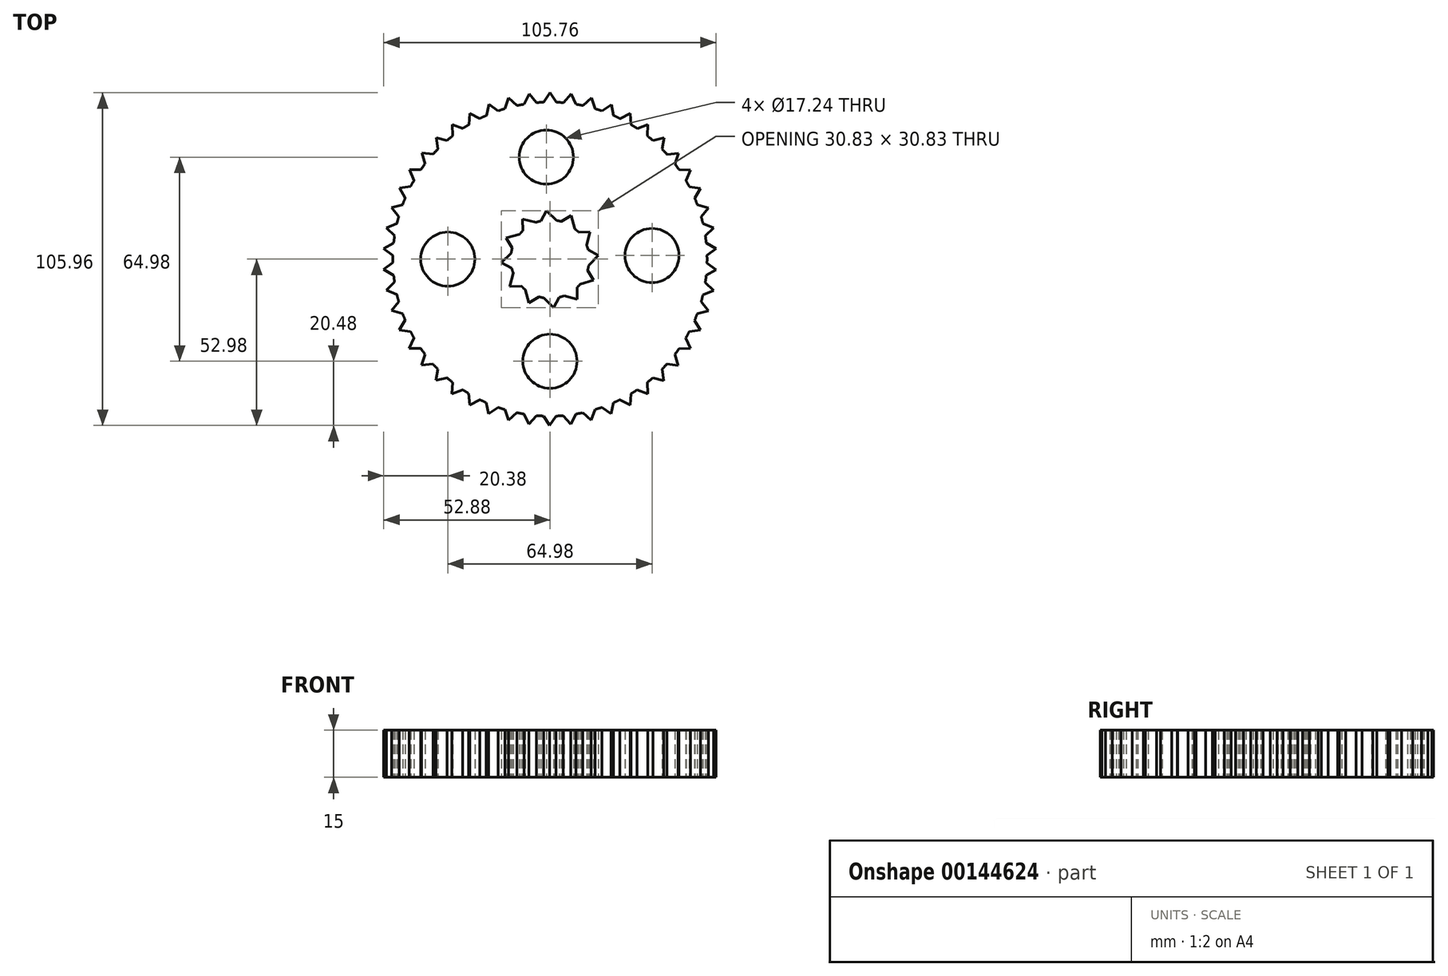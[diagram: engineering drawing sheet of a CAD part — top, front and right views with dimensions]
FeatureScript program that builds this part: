
annotation { "Feature Type Name" : "Feature", "Feature Type Description" : "" }
export const myFeature = defineFeature(function(context is Context, id is Id, definition is map)
    precondition{}
    {
        {
            var Q0;
            Q0=qCreatedBy(makeId("Top.planeOp"),FACE);
            var sketch = newSketch(context, id + "F0", { "sketchPlane" : qUnion([Q0])});
            skArc(sketch, "E0", {"start": v(-1.97, 49.96) * mm, "mid": v(-3.12, 49.9) * mm, "end": v(-4.26, 49.82) * mm});
            skLineSegment(sketch, "E1", {"start": v(-1.97, 49.96) * mm, "end": v(0.05, 52.98) * mm});
            skLineSegment(sketch, "E2", {"start": v(0.05, 52.98) * mm, "end": v(2.02, 49.96) * mm});
            skLineSegment(sketch, "E3.1.0", {"start": v(-8.22, 49.32) * mm, "end": v(-6.6, 52.57) * mm});
            skLineSegment(sketch, "E3.1.1", {"start": v(-6.6, 52.57) * mm, "end": v(-4.26, 49.82) * mm});
            skLineSegment(sketch, "E3.2.0", {"start": v(-14.34, 47.9) * mm, "end": v(-13.13, 51.33) * mm});
            skLineSegment(sketch, "E3.2.1", {"start": v(-13.13, 51.33) * mm, "end": v(-10.47, 48.9) * mm});
            skLineSegment(sketch, "E3.3.0", {"start": v(-20.23, 45.73) * mm, "end": v(-19.46, 49.28) * mm});
            skLineSegment(sketch, "E3.3.1", {"start": v(-19.46, 49.28) * mm, "end": v(-16.51, 47.2) * mm});
            skLineSegment(sketch, "E3.4.0", {"start": v(-25.8, 42.83) * mm, "end": v(-25.48, 46.45) * mm});
            skLineSegment(sketch, "E3.4.1", {"start": v(-25.48, 46.45) * mm, "end": v(-22.3, 44.75) * mm});
            skLineSegment(sketch, "E3.5.0", {"start": v(-30.96, 39.26) * mm, "end": v(-31.1, 42.89) * mm});
            skLineSegment(sketch, "E3.5.1", {"start": v(-31.1, 42.89) * mm, "end": v(-27.73, 41.6) * mm});
            skLineSegment(sketch, "E3.6.0", {"start": v(-35.64, 35.07) * mm, "end": v(-36.23, 38.65) * mm});
            skLineSegment(sketch, "E3.6.1", {"start": v(-36.23, 38.65) * mm, "end": v(-32.73, 37.8) * mm});
            skLineSegment(sketch, "E3.7.0", {"start": v(-39.75, 30.33) * mm, "end": v(-40.8, 33.8) * mm});
            skLineSegment(sketch, "E3.7.1", {"start": v(-40.8, 33.8) * mm, "end": v(-37.2, 33.4) * mm});
            skLineSegment(sketch, "E3.8.0", {"start": v(-43.24, 25.1) * mm, "end": v(-44.7, 28.43) * mm});
            skLineSegment(sketch, "E3.8.1", {"start": v(-44.7, 28.43) * mm, "end": v(-41.1, 28.47) * mm});
            skLineSegment(sketch, "E3.9.0", {"start": v(-46.05, 19.49) * mm, "end": v(-47.92, 22.6) * mm});
            skLineSegment(sketch, "E3.9.1", {"start": v(-47.92, 22.6) * mm, "end": v(-44.34, 23.1) * mm});
            skLineSegment(sketch, "E3.10.0", {"start": v(-48.13, 13.56) * mm, "end": v(-50.37, 16.42) * mm});
            skLineSegment(sketch, "E3.10.1", {"start": v(-50.37, 16.42) * mm, "end": v(-46.9, 17.36) * mm});
            skLineSegment(sketch, "E3.11.0", {"start": v(-49.45, 7.42) * mm, "end": v(-52.03, 9.97) * mm});
            skLineSegment(sketch, "E3.11.1", {"start": v(-52.03, 9.97) * mm, "end": v(-48.7, 11.34) * mm});
            skLineSegment(sketch, "E3.12.0", {"start": v(-49.99, 1.17) * mm, "end": v(-52.87, 3.37) * mm});
            skLineSegment(sketch, "E3.12.1", {"start": v(-52.87, 3.37) * mm, "end": v(-49.73, 5.15) * mm});
            skLineSegment(sketch, "E3.13.0", {"start": v(-49.74, -5.1) * mm, "end": v(-52.88, -3.28) * mm});
            skLineSegment(sketch, "E3.13.1", {"start": v(-52.88, -3.28) * mm, "end": v(-49.99, -1.12) * mm});
            skLineSegment(sketch, "E3.14.0", {"start": v(-48.7, -11.3) * mm, "end": v(-52.05, -9.88) * mm});
            skLineSegment(sketch, "E3.14.1", {"start": v(-52.05, -9.88) * mm, "end": v(-49.45, -7.38) * mm});
            skLineSegment(sketch, "E3.15.0", {"start": v(-46.9, -17.32) * mm, "end": v(-50.4, -16.33) * mm});
            skLineSegment(sketch, "E3.15.1", {"start": v(-50.4, -16.33) * mm, "end": v(-48.14, -13.52) * mm});
            skLineSegment(sketch, "E3.16.0", {"start": v(-44.37, -23.06) * mm, "end": v(-47.96, -22.52) * mm});
            skLineSegment(sketch, "E3.16.1", {"start": v(-47.96, -22.52) * mm, "end": v(-46.06, -19.44) * mm});
            skLineSegment(sketch, "E3.17.0", {"start": v(-41.13, -28.44) * mm, "end": v(-44.76, -28.35) * mm});
            skLineSegment(sketch, "E3.17.1", {"start": v(-44.76, -28.35) * mm, "end": v(-43.26, -25.06) * mm});
            skLineSegment(sketch, "E3.18.0", {"start": v(-37.24, -33.37) * mm, "end": v(-40.85, -33.74) * mm});
            skLineSegment(sketch, "E3.18.1", {"start": v(-40.85, -33.74) * mm, "end": v(-39.78, -30.29) * mm});
            skLineSegment(sketch, "E3.19.0", {"start": v(-32.76, -37.77) * mm, "end": v(-36.3, -38.6) * mm});
            skLineSegment(sketch, "E3.19.1", {"start": v(-36.3, -38.6) * mm, "end": v(-35.67, -35.04) * mm});
            skLineSegment(sketch, "E3.20.0", {"start": v(-27.77, -41.58) * mm, "end": v(-31.18, -42.84) * mm});
            skLineSegment(sketch, "E3.20.1", {"start": v(-31.18, -42.84) * mm, "end": v(-31, -39.23) * mm});
            skLineSegment(sketch, "E3.21.0", {"start": v(-22.34, -44.73) * mm, "end": v(-25.56, -46.4) * mm});
            skLineSegment(sketch, "E3.21.1", {"start": v(-25.56, -46.4) * mm, "end": v(-25.84, -42.8) * mm});
            skLineSegment(sketch, "E3.22.0", {"start": v(-16.56, -47.18) * mm, "end": v(-19.55, -49.24) * mm});
            skLineSegment(sketch, "E3.22.1", {"start": v(-19.55, -49.24) * mm, "end": v(-20.27, -45.7) * mm});
            skLineSegment(sketch, "E3.23.0", {"start": v(-10.51, -48.88) * mm, "end": v(-13.22, -51.3) * mm});
            skLineSegment(sketch, "E3.23.1", {"start": v(-13.22, -51.3) * mm, "end": v(-14.38, -47.89) * mm});
            skLineSegment(sketch, "E3.24.0", {"start": v(-4.3, -49.81) * mm, "end": v(-6.69, -52.56) * mm});
            skLineSegment(sketch, "E3.24.1", {"start": v(-6.69, -52.56) * mm, "end": v(-8.26, -49.31) * mm});
            skLineSegment(sketch, "E3.25.0", {"start": v(1.97, -49.96) * mm, "end": v(-0.05, -52.98) * mm});
            skLineSegment(sketch, "E3.25.1", {"start": v(-0.05, -52.98) * mm, "end": v(-2.02, -49.96) * mm});
            skLineSegment(sketch, "E3.26.0", {"start": v(8.22, -49.32) * mm, "end": v(6.6, -52.57) * mm});
            skLineSegment(sketch, "E3.26.1", {"start": v(6.6, -52.57) * mm, "end": v(4.26, -49.82) * mm});
            skLineSegment(sketch, "E3.27.0", {"start": v(14.34, -47.9) * mm, "end": v(13.13, -51.33) * mm});
            skLineSegment(sketch, "E3.27.1", {"start": v(13.13, -51.33) * mm, "end": v(10.47, -48.9) * mm});
            skLineSegment(sketch, "E3.28.0", {"start": v(20.23, -45.73) * mm, "end": v(19.46, -49.28) * mm});
            skLineSegment(sketch, "E3.28.1", {"start": v(19.46, -49.28) * mm, "end": v(16.51, -47.2) * mm});
            skLineSegment(sketch, "E3.29.0", {"start": v(25.8, -42.83) * mm, "end": v(25.48, -46.45) * mm});
            skLineSegment(sketch, "E3.29.1", {"start": v(25.48, -46.45) * mm, "end": v(22.3, -44.75) * mm});
            skLineSegment(sketch, "E3.30.0", {"start": v(30.96, -39.26) * mm, "end": v(31.1, -42.89) * mm});
            skLineSegment(sketch, "E3.30.1", {"start": v(31.1, -42.89) * mm, "end": v(27.73, -41.6) * mm});
            skLineSegment(sketch, "E3.31.0", {"start": v(35.64, -35.07) * mm, "end": v(36.23, -38.65) * mm});
            skLineSegment(sketch, "E3.31.1", {"start": v(36.23, -38.65) * mm, "end": v(32.73, -37.8) * mm});
            skLineSegment(sketch, "E3.32.0", {"start": v(39.75, -30.33) * mm, "end": v(40.8, -33.8) * mm});
            skLineSegment(sketch, "E3.32.1", {"start": v(40.8, -33.8) * mm, "end": v(37.2, -33.4) * mm});
            skLineSegment(sketch, "E3.33.0", {"start": v(43.24, -25.1) * mm, "end": v(44.7, -28.43) * mm});
            skLineSegment(sketch, "E3.33.1", {"start": v(44.7, -28.43) * mm, "end": v(41.1, -28.47) * mm});
            skLineSegment(sketch, "E3.34.0", {"start": v(46.05, -19.49) * mm, "end": v(47.92, -22.6) * mm});
            skLineSegment(sketch, "E3.34.1", {"start": v(47.92, -22.6) * mm, "end": v(44.34, -23.1) * mm});
            skLineSegment(sketch, "E3.35.0", {"start": v(48.13, -13.56) * mm, "end": v(50.37, -16.42) * mm});
            skLineSegment(sketch, "E3.35.1", {"start": v(50.37, -16.42) * mm, "end": v(46.9, -17.36) * mm});
            skLineSegment(sketch, "E3.36.0", {"start": v(49.45, -7.42) * mm, "end": v(52.03, -9.97) * mm});
            skLineSegment(sketch, "E3.36.1", {"start": v(52.03, -9.97) * mm, "end": v(48.7, -11.34) * mm});
            skLineSegment(sketch, "E3.37.0", {"start": v(49.99, -1.17) * mm, "end": v(52.87, -3.37) * mm});
            skLineSegment(sketch, "E3.37.1", {"start": v(52.87, -3.37) * mm, "end": v(49.73, -5.15) * mm});
            skLineSegment(sketch, "E3.38.0", {"start": v(49.74, 5.1) * mm, "end": v(52.88, 3.28) * mm});
            skLineSegment(sketch, "E3.38.1", {"start": v(52.88, 3.28) * mm, "end": v(49.99, 1.12) * mm});
            skLineSegment(sketch, "E3.39.0", {"start": v(48.7, 11.3) * mm, "end": v(52.05, 9.88) * mm});
            skLineSegment(sketch, "E3.39.1", {"start": v(52.05, 9.88) * mm, "end": v(49.45, 7.38) * mm});
            skLineSegment(sketch, "E3.40.0", {"start": v(46.9, 17.32) * mm, "end": v(50.4, 16.33) * mm});
            skLineSegment(sketch, "E3.40.1", {"start": v(50.4, 16.33) * mm, "end": v(48.14, 13.52) * mm});
            skLineSegment(sketch, "E3.41.0", {"start": v(44.37, 23.06) * mm, "end": v(47.96, 22.52) * mm});
            skLineSegment(sketch, "E3.41.1", {"start": v(47.96, 22.52) * mm, "end": v(46.06, 19.44) * mm});
            skLineSegment(sketch, "E3.42.0", {"start": v(41.13, 28.44) * mm, "end": v(44.76, 28.35) * mm});
            skLineSegment(sketch, "E3.42.1", {"start": v(44.76, 28.35) * mm, "end": v(43.26, 25.06) * mm});
            skLineSegment(sketch, "E3.43.0", {"start": v(37.24, 33.37) * mm, "end": v(40.85, 33.74) * mm});
            skLineSegment(sketch, "E3.43.1", {"start": v(40.85, 33.74) * mm, "end": v(39.78, 30.29) * mm});
            skLineSegment(sketch, "E3.44.0", {"start": v(32.76, 37.77) * mm, "end": v(36.3, 38.6) * mm});
            skLineSegment(sketch, "E3.44.1", {"start": v(36.3, 38.6) * mm, "end": v(35.67, 35.04) * mm});
            skLineSegment(sketch, "E3.45.0", {"start": v(27.77, 41.58) * mm, "end": v(31.18, 42.84) * mm});
            skLineSegment(sketch, "E3.45.1", {"start": v(31.18, 42.84) * mm, "end": v(31, 39.23) * mm});
            skLineSegment(sketch, "E3.46.0", {"start": v(22.34, 44.73) * mm, "end": v(25.56, 46.4) * mm});
            skLineSegment(sketch, "E3.46.1", {"start": v(25.56, 46.4) * mm, "end": v(25.84, 42.8) * mm});
            skLineSegment(sketch, "E3.47.0", {"start": v(16.56, 47.18) * mm, "end": v(19.55, 49.24) * mm});
            skLineSegment(sketch, "E3.47.1", {"start": v(19.55, 49.24) * mm, "end": v(20.27, 45.7) * mm});
            skLineSegment(sketch, "E3.48.0", {"start": v(10.51, 48.88) * mm, "end": v(13.22, 51.3) * mm});
            skLineSegment(sketch, "E3.48.1", {"start": v(13.22, 51.3) * mm, "end": v(14.38, 47.89) * mm});
            skLineSegment(sketch, "E3.49.0", {"start": v(4.3, 49.81) * mm, "end": v(6.69, 52.56) * mm});
            skLineSegment(sketch, "E3.49.1", {"start": v(6.69, 52.56) * mm, "end": v(8.26, 49.31) * mm});
            skArc(sketch, "E4.trimOffspring", {"start": v(4.3, 49.81) * mm, "mid": v(3.16, 49.9) * mm, "end": v(2.02, 49.96) * mm});
            skArc(sketch, "E5.trimOffspring", {"start": v(10.51, 48.88) * mm, "mid": v(9.4, 49.11) * mm, "end": v(8.26, 49.31) * mm});
            skArc(sketch, "E6.trimOffspring", {"start": v(16.56, 47.18) * mm, "mid": v(15.47, 47.55) * mm, "end": v(14.38, 47.89) * mm});
            skArc(sketch, "E7.trimOffspring", {"start": v(-8.22, 49.32) * mm, "mid": v(-9.35, 49.12) * mm, "end": v(-10.47, 48.9) * mm});
            skArc(sketch, "E8.trimOffspring", {"start": v(-14.34, 47.9) * mm, "mid": v(-15.43, 47.56) * mm, "end": v(-16.51, 47.2) * mm});
            skArc(sketch, "E9.trimOffspring", {"start": v(-20.23, 45.73) * mm, "mid": v(-21.27, 45.25) * mm, "end": v(-22.3, 44.75) * mm});
            skArc(sketch, "E10.trimOffspring", {"start": v(-25.8, 42.83) * mm, "mid": v(-26.77, 42.23) * mm, "end": v(-27.73, 41.6) * mm});
            skArc(sketch, "E11.trimOffspring", {"start": v(-30.96, 39.26) * mm, "mid": v(-31.85, 38.54) * mm, "end": v(-32.73, 37.8) * mm});
            skArc(sketch, "E12.trimOffspring", {"start": v(-35.64, 35.07) * mm, "mid": v(-36.43, 34.24) * mm, "end": v(-37.2, 33.4) * mm});
            skArc(sketch, "E13.trimOffspring", {"start": v(-39.75, 30.33) * mm, "mid": v(-40.44, 29.4) * mm, "end": v(-41.1, 28.47) * mm});
            skArc(sketch, "E14.trimOffspring", {"start": v(22.34, 44.73) * mm, "mid": v(21.3, 45.23) * mm, "end": v(20.27, 45.7) * mm});
            skArc(sketch, "E15.trimOffspring", {"start": v(27.77, 41.58) * mm, "mid": v(26.81, 42.2) * mm, "end": v(25.84, 42.8) * mm});
            skArc(sketch, "E16.trimOffspring", {"start": v(32.76, 37.77) * mm, "mid": v(31.89, 38.51) * mm, "end": v(31, 39.23) * mm});
            skArc(sketch, "E17.trimOffspring", {"start": v(37.24, 33.37) * mm, "mid": v(36.46, 34.21) * mm, "end": v(35.67, 35.04) * mm});
            skArc(sketch, "E18.trimOffspring", {"start": v(41.13, 28.44) * mm, "mid": v(40.46, 29.37) * mm, "end": v(39.78, 30.29) * mm});
            skArc(sketch, "E19.trimOffspring", {"start": v(44.37, 23.06) * mm, "mid": v(43.83, 24.07) * mm, "end": v(43.26, 25.06) * mm});
            skArc(sketch, "E20.trimOffspring", {"start": v(46.9, 17.32) * mm, "mid": v(46.5, 18.39) * mm, "end": v(46.06, 19.44) * mm});
            skArc(sketch, "E21.trimOffspring", {"start": v(48.7, 11.3) * mm, "mid": v(48.43, 12.41) * mm, "end": v(48.14, 13.52) * mm});
            skArc(sketch, "E22.trimOffspring", {"start": v(49.74, 5.1) * mm, "mid": v(49.6, 6.24) * mm, "end": v(49.45, 7.38) * mm});
            skArc(sketch, "E23.trimOffspring", {"start": v(-43.24, 25.1) * mm, "mid": v(-43.8, 24.1) * mm, "end": v(-44.34, 23.1) * mm});
            skArc(sketch, "E24.trimOffspring", {"start": v(-46.05, 19.49) * mm, "mid": v(-46.48, 18.43) * mm, "end": v(-46.9, 17.36) * mm});
            skArc(sketch, "E25.trimOffspring", {"start": v(-48.13, 13.56) * mm, "mid": v(-48.42, 12.46) * mm, "end": v(-48.7, 11.34) * mm});
            skArc(sketch, "E26.trimOffspring", {"start": v(-49.45, 7.42) * mm, "mid": v(-49.6, 6.29) * mm, "end": v(-49.73, 5.15) * mm});
            skArc(sketch, "E27.trimOffspring", {"start": v(-49.99, 1.17) * mm, "mid": v(-50, 0.02) * mm, "end": v(-49.99, -1.12) * mm});
            skArc(sketch, "E28.trimOffspring", {"start": v(-49.74, -5.1) * mm, "mid": v(-49.6, -6.24) * mm, "end": v(-49.45, -7.38) * mm});
            skArc(sketch, "E29.trimOffspring", {"start": v(-48.7, -11.3) * mm, "mid": v(-48.43, -12.41) * mm, "end": v(-48.14, -13.52) * mm});
            skArc(sketch, "E30.trimOffspring", {"start": v(-46.9, -17.32) * mm, "mid": v(-46.5, -18.39) * mm, "end": v(-46.06, -19.44) * mm});
            skArc(sketch, "E31.trimOffspring", {"start": v(-44.37, -23.06) * mm, "mid": v(-43.83, -24.07) * mm, "end": v(-43.26, -25.06) * mm});
            skArc(sketch, "E32.trimOffspring", {"start": v(-41.13, -28.44) * mm, "mid": v(-40.46, -29.37) * mm, "end": v(-39.78, -30.29) * mm});
            skArc(sketch, "E33.trimOffspring", {"start": v(-37.24, -33.37) * mm, "mid": v(-36.46, -34.21) * mm, "end": v(-35.67, -35.04) * mm});
            skArc(sketch, "E34.trimOffspring", {"start": v(-32.76, -37.77) * mm, "mid": v(-31.89, -38.51) * mm, "end": v(-31, -39.23) * mm});
            skArc(sketch, "E35.trimOffspring", {"start": v(-27.77, -41.58) * mm, "mid": v(-26.81, -42.2) * mm, "end": v(-25.84, -42.8) * mm});
            skArc(sketch, "E36.trimOffspring", {"start": v(-22.34, -44.73) * mm, "mid": v(-21.3, -45.23) * mm, "end": v(-20.27, -45.7) * mm});
            skArc(sketch, "E37.trimOffspring", {"start": v(-16.56, -47.18) * mm, "mid": v(-15.47, -47.55) * mm, "end": v(-14.38, -47.89) * mm});
            skArc(sketch, "E38.trimOffspring", {"start": v(-10.51, -48.88) * mm, "mid": v(-9.4, -49.11) * mm, "end": v(-8.26, -49.31) * mm});
            skArc(sketch, "E39.trimOffspring", {"start": v(-4.3, -49.81) * mm, "mid": v(-3.16, -49.9) * mm, "end": v(-2.02, -49.96) * mm});
            skArc(sketch, "E40.trimOffspring", {"start": v(1.97, -49.96) * mm, "mid": v(3.12, -49.9) * mm, "end": v(4.26, -49.82) * mm});
            skArc(sketch, "E41.trimOffspring", {"start": v(8.22, -49.32) * mm, "mid": v(9.35, -49.12) * mm, "end": v(10.47, -48.9) * mm});
            skArc(sketch, "E42.trimOffspring", {"start": v(14.34, -47.9) * mm, "mid": v(15.43, -47.56) * mm, "end": v(16.51, -47.2) * mm});
            skArc(sketch, "E43.trimOffspring", {"start": v(20.23, -45.73) * mm, "mid": v(21.27, -45.25) * mm, "end": v(22.3, -44.75) * mm});
            skArc(sketch, "E44.trimOffspring", {"start": v(25.8, -42.83) * mm, "mid": v(26.77, -42.23) * mm, "end": v(27.73, -41.6) * mm});
            skArc(sketch, "E45.trimOffspring", {"start": v(30.96, -39.26) * mm, "mid": v(31.85, -38.54) * mm, "end": v(32.73, -37.8) * mm});
            skArc(sketch, "E46.trimOffspring", {"start": v(35.64, -35.07) * mm, "mid": v(36.43, -34.24) * mm, "end": v(37.2, -33.4) * mm});
            skArc(sketch, "E47.trimOffspring", {"start": v(39.75, -30.33) * mm, "mid": v(40.44, -29.4) * mm, "end": v(41.1, -28.47) * mm});
            skArc(sketch, "E48.trimOffspring", {"start": v(43.24, -25.1) * mm, "mid": v(43.8, -24.1) * mm, "end": v(44.34, -23.1) * mm});
            skArc(sketch, "E49.trimOffspring", {"start": v(46.05, -19.49) * mm, "mid": v(46.48, -18.43) * mm, "end": v(46.9, -17.36) * mm});
            skArc(sketch, "E50.trimOffspring", {"start": v(48.13, -13.56) * mm, "mid": v(48.42, -12.46) * mm, "end": v(48.7, -11.34) * mm});
            skArc(sketch, "E51.trimOffspring", {"start": v(49.45, -7.42) * mm, "mid": v(49.6, -6.29) * mm, "end": v(49.73, -5.15) * mm});
            skArc(sketch, "E52.trimOffspring", {"start": v(49.99, -1.17) * mm, "mid": v(50, -0.02) * mm, "end": v(49.99, 1.12) * mm});
            skArc(sketch, "E53", {"start": v(-2.92, 12.15) * mm, "mid": v(-3.69, 11.94) * mm, "end": v(-4.44, 11.69) * mm});
            skLineSegment(sketch, "E54", {"start": v(-2.92, 12.15) * mm, "end": v(-1.15, 15.42) * mm});
            skLineSegment(sketch, "E55", {"start": v(-1.15, 15.42) * mm, "end": v(2, 12.34) * mm});
            skLineSegment(sketch, "E56.1.0", {"start": v(-8.6, 9.06) * mm, "end": v(-8.7, 12.77) * mm});
            skLineSegment(sketch, "E56.1.1", {"start": v(-8.7, 12.77) * mm, "end": v(-4.44, 11.69) * mm});
            skLineSegment(sketch, "E56.2.0", {"start": v(-11.99, 3.54) * mm, "end": v(-13.93, 6.7) * mm});
            skLineSegment(sketch, "E56.2.1", {"start": v(-13.93, 6.7) * mm, "end": v(-9.69, 7.9) * mm});
            skLineSegment(sketch, "E56.3.0", {"start": v(-12.15, -2.92) * mm, "end": v(-15.42, -1.15) * mm});
            skLineSegment(sketch, "E56.3.1", {"start": v(-15.42, -1.15) * mm, "end": v(-12.34, 2) * mm});
            skLineSegment(sketch, "E56.4.0", {"start": v(-9.06, -8.6) * mm, "end": v(-12.77, -8.7) * mm});
            skLineSegment(sketch, "E56.4.1", {"start": v(-12.77, -8.7) * mm, "end": v(-11.69, -4.44) * mm});
            skLineSegment(sketch, "E56.5.0", {"start": v(-3.54, -11.99) * mm, "end": v(-6.7, -13.93) * mm});
            skLineSegment(sketch, "E56.5.1", {"start": v(-6.7, -13.93) * mm, "end": v(-7.9, -9.69) * mm});
            skLineSegment(sketch, "E56.6.0", {"start": v(2.92, -12.15) * mm, "end": v(1.15, -15.42) * mm});
            skLineSegment(sketch, "E56.6.1", {"start": v(1.15, -15.42) * mm, "end": v(-2, -12.34) * mm});
            skLineSegment(sketch, "E56.7.0", {"start": v(8.6, -9.06) * mm, "end": v(8.7, -12.77) * mm});
            skLineSegment(sketch, "E56.7.1", {"start": v(8.7, -12.77) * mm, "end": v(4.44, -11.69) * mm});
            skLineSegment(sketch, "E56.8.0", {"start": v(11.99, -3.54) * mm, "end": v(13.93, -6.7) * mm});
            skLineSegment(sketch, "E56.8.1", {"start": v(13.93, -6.7) * mm, "end": v(9.69, -7.9) * mm});
            skLineSegment(sketch, "E56.9.0", {"start": v(12.15, 2.92) * mm, "end": v(15.42, 1.15) * mm});
            skLineSegment(sketch, "E56.9.1", {"start": v(15.42, 1.15) * mm, "end": v(12.34, -2) * mm});
            skLineSegment(sketch, "E56.10.0", {"start": v(9.06, 8.6) * mm, "end": v(12.77, 8.7) * mm});
            skLineSegment(sketch, "E56.10.1", {"start": v(12.77, 8.7) * mm, "end": v(11.69, 4.44) * mm});
            skLineSegment(sketch, "E56.11.0", {"start": v(3.54, 11.99) * mm, "end": v(6.7, 13.93) * mm});
            skLineSegment(sketch, "E56.11.1", {"start": v(6.7, 13.93) * mm, "end": v(7.9, 9.69) * mm});
            skArc(sketch, "E57.trimOffspring", {"start": v(3.54, 11.99) * mm, "mid": v(2.78, 12.19) * mm, "end": v(2, 12.34) * mm});
            skArc(sketch, "E58.trimOffspring", {"start": v(9.06, 8.6) * mm, "mid": v(8.5, 9.17) * mm, "end": v(7.9, 9.69) * mm});
            skArc(sketch, "E59.trimOffspring", {"start": v(12.15, 2.92) * mm, "mid": v(11.94, 3.69) * mm, "end": v(11.69, 4.44) * mm});
            skArc(sketch, "E60.trimOffspring", {"start": v(11.99, -3.54) * mm, "mid": v(12.19, -2.78) * mm, "end": v(12.34, -2) * mm});
            skArc(sketch, "E61.trimOffspring", {"start": v(8.6, -9.06) * mm, "mid": v(9.17, -8.5) * mm, "end": v(9.69, -7.9) * mm});
            skArc(sketch, "E62.trimOffspring", {"start": v(2.92, -12.15) * mm, "mid": v(3.69, -11.94) * mm, "end": v(4.44, -11.69) * mm});
            skArc(sketch, "E63.trimOffspring", {"start": v(-3.54, -11.99) * mm, "mid": v(-2.78, -12.19) * mm, "end": v(-2, -12.34) * mm});
            skArc(sketch, "E64.trimOffspring", {"start": v(-8.6, 9.06) * mm, "mid": v(-9.17, 8.5) * mm, "end": v(-9.69, 7.9) * mm});
            skArc(sketch, "E65.trimOffspring", {"start": v(-11.99, 3.54) * mm, "mid": v(-12.19, 2.78) * mm, "end": v(-12.34, 2) * mm});
            skArc(sketch, "E66.trimOffspring", {"start": v(-12.15, -2.92) * mm, "mid": v(-11.94, -3.69) * mm, "end": v(-11.69, -4.44) * mm});
            skArc(sketch, "E67.trimOffspring", {"start": v(-9.06, -8.6) * mm, "mid": v(-8.5, -9.17) * mm, "end": v(-7.9, -9.69) * mm});
            skCircle(sketch, "E68", {"center": v(-32.5, 0) * mm, "radius": 8.62 * mm});
            skCircle(sketch, "E69", {"center": v(32.48, 1.15) * mm, "radius": 8.62 * mm});
            skCircle(sketch, "E70", {"center": v(-1.15, 32.48) * mm, "radius": 8.62 * mm});
            skCircle(sketch, "E71", {"center": v(0, -32.5) * mm, "radius": 8.62 * mm});
            skSolve(sketch);
        }
        {
            var Q0;
            Q0 = qSketchRegion(id + "F0", true);
            extrude(context, id + "F1", {"entities" : qUnion([Q0]), "endBound" : BoundingType.SYMMETRIC, "depth" : 15 * mm});
        }
    });
